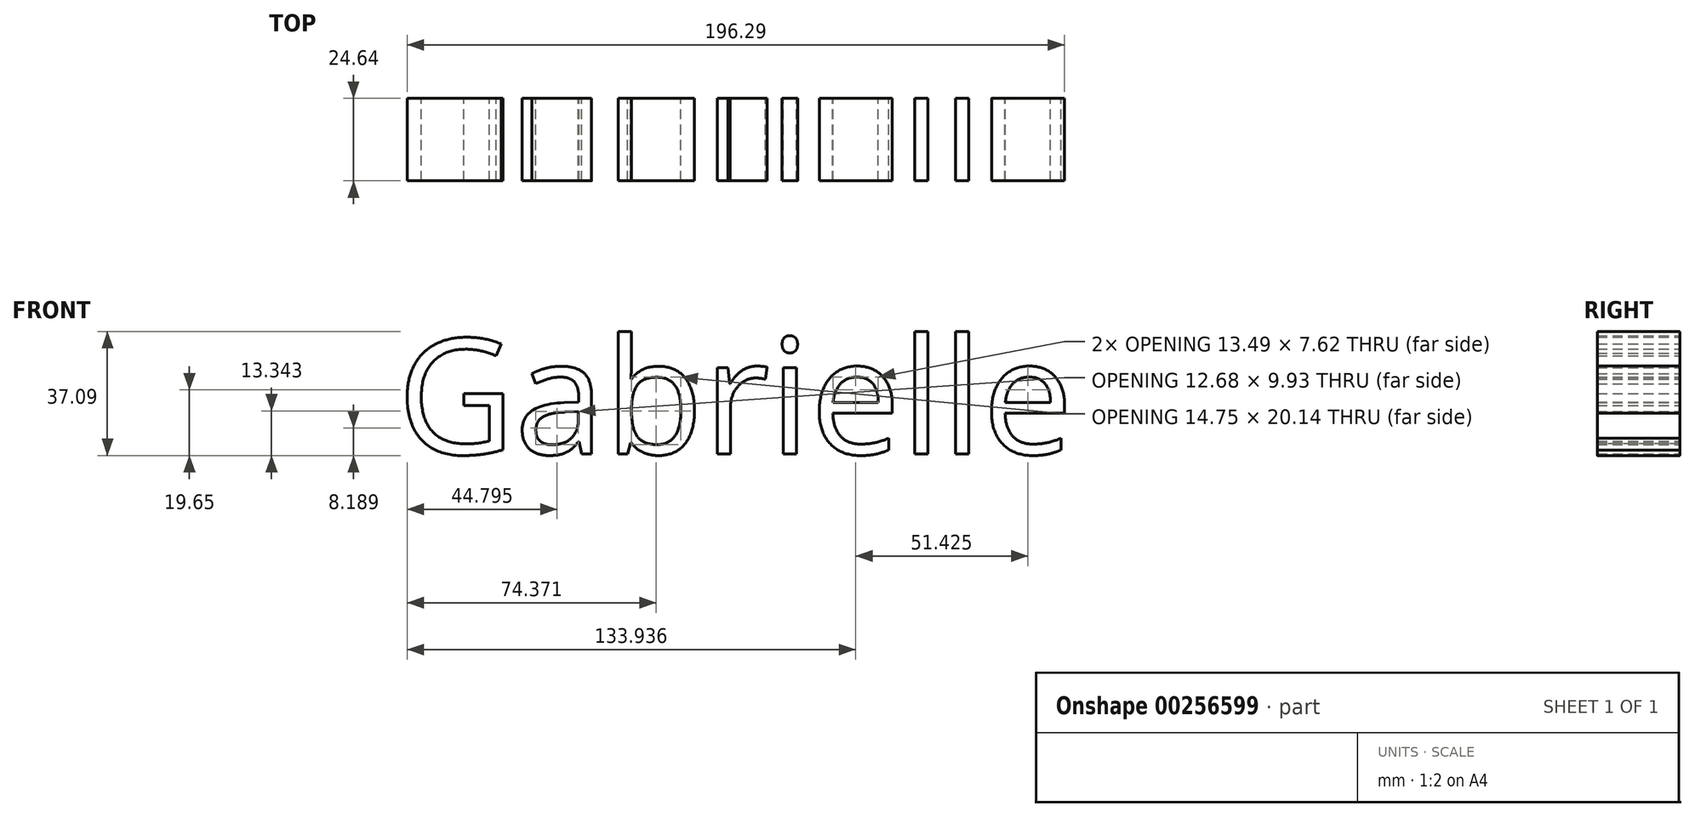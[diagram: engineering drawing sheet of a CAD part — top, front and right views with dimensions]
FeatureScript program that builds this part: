
annotation { "Feature Type Name" : "Feature", "Feature Type Description" : "" }
export const myFeature = defineFeature(function(context is Context, id is Id, definition is map)
    precondition{}
    {
        {
            var Q0;
            Q0=qCreatedBy(makeId("Front.planeOp"),FACE);
            var sketch = newSketch(context, id + "F0", { "sketchPlane" : qUnion([Q0])});
            skText(sketch, "E0", { "text": "Gabrielle\n", "fontName": "OpenSans-Regular.ttf"});
            const initialGuessF0  = {"E0": [-0.1507, -0.0176, 1, 0, 0.0347]};
            skSetInitialGuess(sketch, initialGuessF0);
            skSolve(sketch);
        }
        {
            var Q0;
            Q0 = qSketchRegion(id + "F0", true);
            extrude(context, id + "F1", {"entities" : qUnion([Q0]), "depth" : 24.64 * mm});
        }
    });
